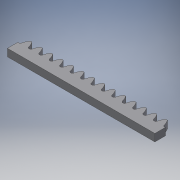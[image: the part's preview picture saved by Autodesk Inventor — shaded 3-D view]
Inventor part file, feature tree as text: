
AUTODESK INVENTOR PART (.ipt)
format: ipt  version: 2017 (Build 210142000, 142)  size: 215,552 bytes
history: native  units: mm
features: sketch x5, extrude x5, other x2, pattern_linear x1, fillet x1, projected_geometry x1, reference x1
ambient origin geometry x8: Origin, YZ Plane, XZ Plane, XY Plane, X Axis, Y Axis, Z Axis, Center Point
bodies: Body1 (feature_tree)
feature tree (16):
  sketch  "Sketch1"  dims[d2=100.0mm d3=12.0mm]
  extrude  "Extrusion2"  Depth=12.0mm
  extrude  "Extrusion3"  Depth=5.0mm
  pattern_linear  "Rectangular Pattern1"  Count1=15 Spacing1=7.065mm
  extrude  "Extrusion4"  Depth=2.0mm
  extrude  "Extrusion5"  Depth=10.0mm TaperAngle=0.0deg
  fillet  "Fillet1"  Radius=4.3mm
  extrude  "Extrusion6"  Depth=10.0mm TaperAngle=0.0deg
  sketch  "Sketch2"  dims[d4=5.0mm d5=0.0mm d6=5.0mm]
  sketch  "Sketch3"  dims[d7=0.0mm d8=0.0mm d9=150.0mm d11=7.065mm]
  projected_geometry  "Projected Loop1"
  sketch  "Sketch4"  dims[d12=7.0mm d13=2.0mm]
  reference  "Reference1"
  sketch  "Sketch5"  dims[d14=18.0mm d15=10.0mm d16=0.0mm d17=4.3mm d18=10.0mm d19=0.0mm d20=6.0mm d21=10.0mm d22=0.0mm]
  other  "Assembly2.iam"
  other  "frame:1"
